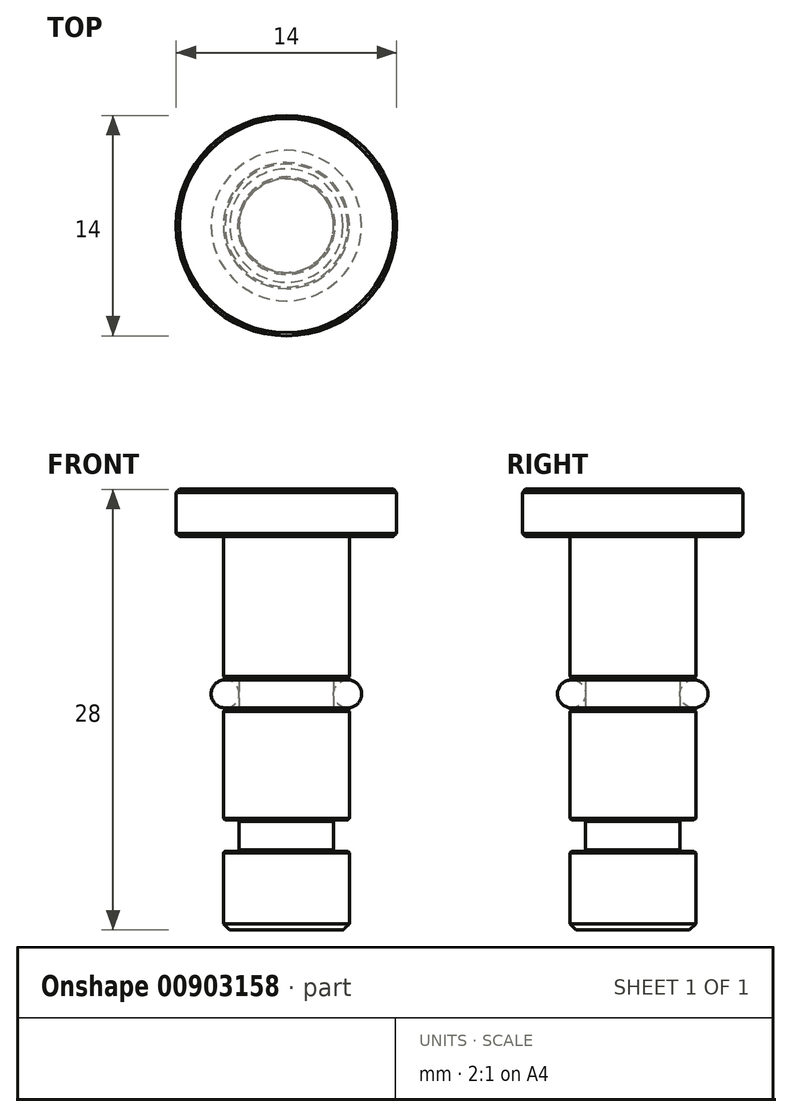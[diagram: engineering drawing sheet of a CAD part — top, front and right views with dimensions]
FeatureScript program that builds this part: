
annotation { "Feature Type Name" : "Feature", "Feature Type Description" : "" }
export const myFeature = defineFeature(function(context is Context, id is Id, definition is map)
    precondition{}
    {
        {
            var Q0;
            Q0=qCreatedBy(makeId("Front.planeOp"),FACE);
            var sketch = newSketch(context, id + "F0", { "sketchPlane" : qUnion([Q0])});
            skLineSegment(sketch, "E0", {"start": v(0, 17.32) * mm, "end": v(7, 17.32) * mm});
            skLineSegment(sketch, "E1", {"start": v(7, 17.32) * mm, "end": v(7, 14.32) * mm});
            skLineSegment(sketch, "E2", {"start": v(7, 14.32) * mm, "end": v(4, 14.32) * mm});
            skLineSegment(sketch, "E3", {"start": v(4, 14.32) * mm, "end": v(4, 5.32) * mm});
            skLineSegment(sketch, "E4", {"start": v(4, -10.68) * mm, "end": v(0, -10.68) * mm});
            skLineSegment(sketch, "E5", {"start": v(0, -10.68) * mm, "end": v(0, 17.32) * mm});
            skLineSegment(sketch, "E6", {"start": v(4, 5.32) * mm, "end": v(3, 5.32) * mm});
            skLineSegment(sketch, "E7", {"start": v(3, 5.32) * mm, "end": v(3, 3.32) * mm});
            skLineSegment(sketch, "E8", {"start": v(3, 3.32) * mm, "end": v(4, 3.32) * mm});
            skLineSegment(sketch, "E9.trimOffspring", {"start": v(4, 3.32) * mm, "end": v(4, -3.68) * mm});
            skLineSegment(sketch, "E10", {"start": v(4, -3.68) * mm, "end": v(3, -3.68) * mm});
            skLineSegment(sketch, "E11", {"start": v(3, -3.68) * mm, "end": v(3, -5.68) * mm});
            skLineSegment(sketch, "E12", {"start": v(3, -5.68) * mm, "end": v(4, -5.68) * mm});
            skLineSegment(sketch, "E13.trimOffspring", {"start": v(4, -5.68) * mm, "end": v(4, -10.68) * mm});
            skCircle(sketch, "E14", {"center": v(3.89, 4.32) * mm, "radius": 0.89 * mm});
            skSolve(sketch);
        }
        {
            var Q0;
            Q0 = qSketchRegion(id + "F0", true);
            var Q1;
            Q1=sQuery(id+"F0.wireOp",EDGE,"E5");
            revolve(context, id + "F1", {"surfaceOperationType" : NewSurfaceOperationType.NEW, "entities" : qUnion([Q0]), "axis" : qUnion([Q1]), "revolveType" : RevolveType.FULL});
        }
        {
            var Q0;
            Q0=makeQuery(id+"F1.opRevolve","SWEPT_FACE",FACE,{"disambiguationData":[OSD([sQuery(id+"F0.wireOp",EDGE,"E6")])]});
            chamfer(context, id + "F2", {"entities" : qUnion([Q0]), "width" : 0.1 * mm, "tangentPropagation" : true});
        }
        {
            var Q0;
            Q0=makeQuery(id+"F1.opRevolve","SWEPT_EDGE",EDGE,{"disambiguationData":[OSD([sQuery(id+"F0.wireOp",EDGE,"E8"),sQuery(id+"F0.wireOp",EDGE,"E9.trimOffspring")])]});
            var Q1;
            Q1=makeQuery(id+"F1.opRevolve","SWEPT_EDGE",EDGE,{"disambiguationData":[OSD([sQuery(id+"F0.wireOp",EDGE,"E9.trimOffspring"),sQuery(id+"F0.wireOp",EDGE,"E10")])]});
            var Q2;
            Q2=makeQuery(id+"F1.opRevolve","SWEPT_EDGE",EDGE,{"disambiguationData":[OSD([sQuery(id+"F0.wireOp",EDGE,"E12"),sQuery(id+"F0.wireOp",EDGE,"E13.trimOffspring")])]});
            var Q3;
            Q3=makeQuery(id+"F1.opRevolve","SWEPT_EDGE",EDGE,{"disambiguationData":[OSD([sQuery(id+"F0.wireOp",EDGE,"E7"),sQuery(id+"F0.wireOp",EDGE,"E8")])]});
            var Q4;
            Q4=makeQuery(id+"F1.opRevolve","SWEPT_EDGE",EDGE,{"disambiguationData":[OSD([sQuery(id+"F0.wireOp",EDGE,"E11"),sQuery(id+"F0.wireOp",EDGE,"E12")])]});
            var Q5;
            Q5=makeQuery(id+"F1.opRevolve","SWEPT_EDGE",EDGE,{"disambiguationData":[OSD([sQuery(id+"F0.wireOp",EDGE,"E10"),sQuery(id+"F0.wireOp",EDGE,"E11")])]});
            chamfer(context, id + "F3", {"entities" : qUnion([Q0, Q1, Q2, Q3, Q4, Q5]), "width" : 0.1 * mm, "tangentPropagation" : true});
        }
        {
            var Q0;
            Q0=makeQuery(id+"F1.opRevolve","SWEPT_EDGE",EDGE,{"disambiguationData":[OSD([sQuery(id+"F0.wireOp",EDGE,"E0"),sQuery(id+"F0.wireOp",EDGE,"E1")])]});
            var Q1;
            Q1=makeQuery(id+"F1.opRevolve","SWEPT_EDGE",EDGE,{"disambiguationData":[OSD([sQuery(id+"F0.wireOp",EDGE,"E1"),sQuery(id+"F0.wireOp",EDGE,"E2")])]});
            chamfer(context, id + "F4", {"entities" : qUnion([Q0, Q1]), "width" : 0.2 * mm, "tangentPropagation" : true});
        }
        {
            var Q0;
            Q0=makeQuery(id+"F1.opRevolve","SWEPT_EDGE",EDGE,{"disambiguationData":[OSD([sQuery(id+"F0.wireOp",EDGE,"E4"),sQuery(id+"F0.wireOp",EDGE,"E13.trimOffspring")])]});
            chamfer(context, id + "F5", {"entities" : qUnion([Q0]), "width" : 0.4 * mm, "tangentPropagation" : true});
        }
    });
